# Revit family: MSU-DFX
name_source: partatom
category: Lighting Fixtures
units: mm (PartAtom-declared; Revit-internal decimal feet)

## family parameters
Always vertical = Yes
Cut with Voids When Loaded = No
Host = Ceiling
Light Source = Yes
OmniClass Number = 23.80.70.11.14.17
OmniClass Title = Direct/Indirect
Part Type = Normal
Room Calculation Point = No
Round Connector Dimension = Use Diameter
Shared = No

## types (27) — shared parameters
Assembly Code = D5020200
Color Filter = 16777215
Description = LED Recessed Surgical with 365DisInFx UVA Technology
Dimming Lamp Color Temperature Shift = <None>
Emit Shape Visible in Rendering = No
Emit from Rectangle Width = 1' - 11 3/4"
Housing Finish = Metal - Viscor - White
Lamp = LED
Lens Finish = Acrylic - Viscor - Frosted Prismatic P12
Manufacturer = CERTOLUX by VISCOR
Model = MSU-DFX
Tilt Angle = 90.00°
URL = https://www.viscor.com
Voltage = 120 V
Width = 1' - 11 3/4"

## per-type parameters (varying)
| type | Apparent Load | Emit from Rectangle Length | Lamp Wattage | Length | Photometric Web File |
| MSU-DFX2X2-LED840K100Lxxx-DSA | 84 VA | 1' - 11 3/4" | 84 VA | 1' - 11 3/4" | MSU-DFX2X2-LED840K100Lxxx-DSA.ies |
| MSU-DFX2X2-LED840K100Lxxx-ASY | 84 VA | 1' - 11 3/4" | 84 VA | 1' - 11 3/4" | MSU-DFX2X2-LED840K100Lxxx-ASY.ies |
| MSU-DFX2X2-LED840K100Lxxx-FASY | 84 VA | 1' - 11 3/4" | 84 VA | 1' - 11 3/4" | MSU-DFX2X2-LED840K100Lxxx-FASY.ies |
| MSU-DFX2X4-LED840K100Lxxx-DSA | 81 VA | 3' - 11 3/4" | 81 VA | 3' - 11 3/4" | MSU-DFX2X4-LED840K100Lxxx-DSA.ies |
| MSU-DFX2X4-LED840K100Lxxx-ASY | 81 VA | 3' - 11 3/4" | 81 VA | 3' - 11 3/4" | MSU-DFX2X4-LED840K100Lxxx-ASY.ies |
| MSU-DFX2X4-LED840K100Lxxx-FASY | 81 VA | 3' - 11 3/4" | 81 VA | 3' - 11 3/4" | MSU-DFX2X4-LED840K100Lxxx-FASY.ies |
| MSU-DFX2X2-LED840K035Lxxx-ASY | 28 VA | 1' - 11 3/4" | 28 VA | 1' - 11 3/4" | MSU-DFX2X2-LED840K035Lxxx-ASY.ies |
| MSU-DFX2X2-LED840K055Lxxx-ASY | 45 VA | 1' - 11 3/4" | 45 VA | 1' - 11 3/4" | MSU-DFX2X2-LED840K055Lxxx-ASY.ies |
| MSU-DFX2X2-LED840K070Lxxx-ASY | 59 VA | 1' - 11 3/4" | 59 VA | 1' - 11 3/4" | MSU-DFX2X2-LED840K070Lxxx-ASY.ies |
| MSU-DFX2X2-LED840K035Lxxx-DSA | 28 VA | 1' - 11 3/4" | 28 VA | 1' - 11 3/4" | MSU-DFX2X2-LED840K035Lxxx-DSA.ies |
| MSU-DFX2X2-LED840K055Lxxx-DSA | 45 VA | 1' - 11 3/4" | 45 VA | 1' - 11 3/4" | MSU-DFX2X2-LED840K055Lxxx-DSA.ies |
| MSU-DFX2X2-LED840K070Lxxx-DSA | 59 VA | 1' - 11 3/4" | 59 VA | 1' - 11 3/4" | MSU-DFX2X2-LED840K070Lxxx-DSA.ies |
| MSU-DFX2X2-LED840K035Lxxx-FASY | 28 VA | 1' - 11 3/4" | 28 VA | 1' - 11 3/4" | MSU-DFX2X2-LED840K035Lxxx-FASY.ies |
| MSU-DFX2X2-LED840K055Lxxx-FASY | 45 VA | 1' - 11 3/4" | 45 VA | 1' - 11 3/4" | MSU-DFX2X2-LED840K055Lxxx-FASY.ies |
| MSU-DFX2X2-LED840K070Lxxx-FASY | 59 VA | 1' - 11 3/4" | 59 VA | 1' - 11 3/4" | MSU-DFX2X2-LED840K070Lxxx-FASY.ies |
| MSU-DFX2X4-LED840K055Lxxx-ASY | 43 VA | 3' - 11 3/4" | 43 VA | 3' - 11 3/4" | MSU-DFX2X4-LED840K055Lxxx-ASY.ies |
| MSU-DFX2X4-LED840K070Lxxx-ASY | 55 VA | 3' - 11 3/4" | 55 VA | 3' - 11 3/4" | MSU-DFX2X4-LED840K070Lxxx-ASY.ies |
| MSU-DFX2X4-LED840K120Lxxx-ASY | 98 VA | 3' - 11 3/4" | 98 VA | 3' - 11 3/4" | MSU-DFX2X4-LED840K120Lxxx-ASY.ies |
| MSU-DFX2X4-LED840K180Lxxx-ASY | 149 VA | 3' - 11 3/4" | 149 VA | 3' - 11 3/4" | MSU-DFX2X4-LED840K180Lxxx-ASY.ies |
| MSU-DFX2X4-LED840K055Lxxx-FASY | 43 VA | 3' - 11 3/4" | 43 VA | 3' - 11 3/4" | MSU-DFX2X4-LED840K055Lxxx-FASY.ies |
| MSU-DFX2X4-LED840K070Lxxx-FASY | 55 VA | 3' - 11 3/4" | 55 VA | 3' - 11 3/4" | MSU-DFX2X4-LED840K070Lxxx-FASY.ies |
| MSU-DFX2X4-LED840K120Lxxx-FASY | 98 VA | 3' - 11 3/4" | 98 VA | 3' - 11 3/4" | MSU-DFX2X4-LED840K120Lxxx-FASY.ies |
| MSU-DFX2X4-LED840K180Lxxx-FASY | 149 VA | 3' - 11 3/4" | 149 VA | 3' - 11 3/4" | MSU-DFX2X4-LED840K180Lxxx-FASY.ies |
| MSU-DFX2X4-LED840K055Lxxx-DSA | 43 VA | 3' - 11 3/4" | 43 VA | 3' - 11 3/4" | MSU-DFX2X4-LED840K055Lxxx-DSA.ies |
| MSU-DFX2X4-LED840K070Lxxx-DSA | 55 VA | 3' - 11 3/4" | 55 VA | 3' - 11 3/4" | MSU-DFX2X4-LED840K070Lxxx-DSA.ies |
| MSU-DFX2X4-LED840K120Lxxx-DSA | 98 VA | 3' - 11 3/4" | 98 VA | 3' - 11 3/4" | MSU-DFX2X4-LED840K120Lxxx-DSA.ies |
| MSU-DFX2X4-LED840K180Lxxx-DSA | 149 VA | 3' - 11 3/4" | 149 VA | 3' - 11 3/4" | MSU-DFX2X4-LED840K180Lxxx-DSA.ies |

## geometry (parser evidence)
native form markers: Extrusion x1, Sweep x3
no freeform markers — native parametric forms only
